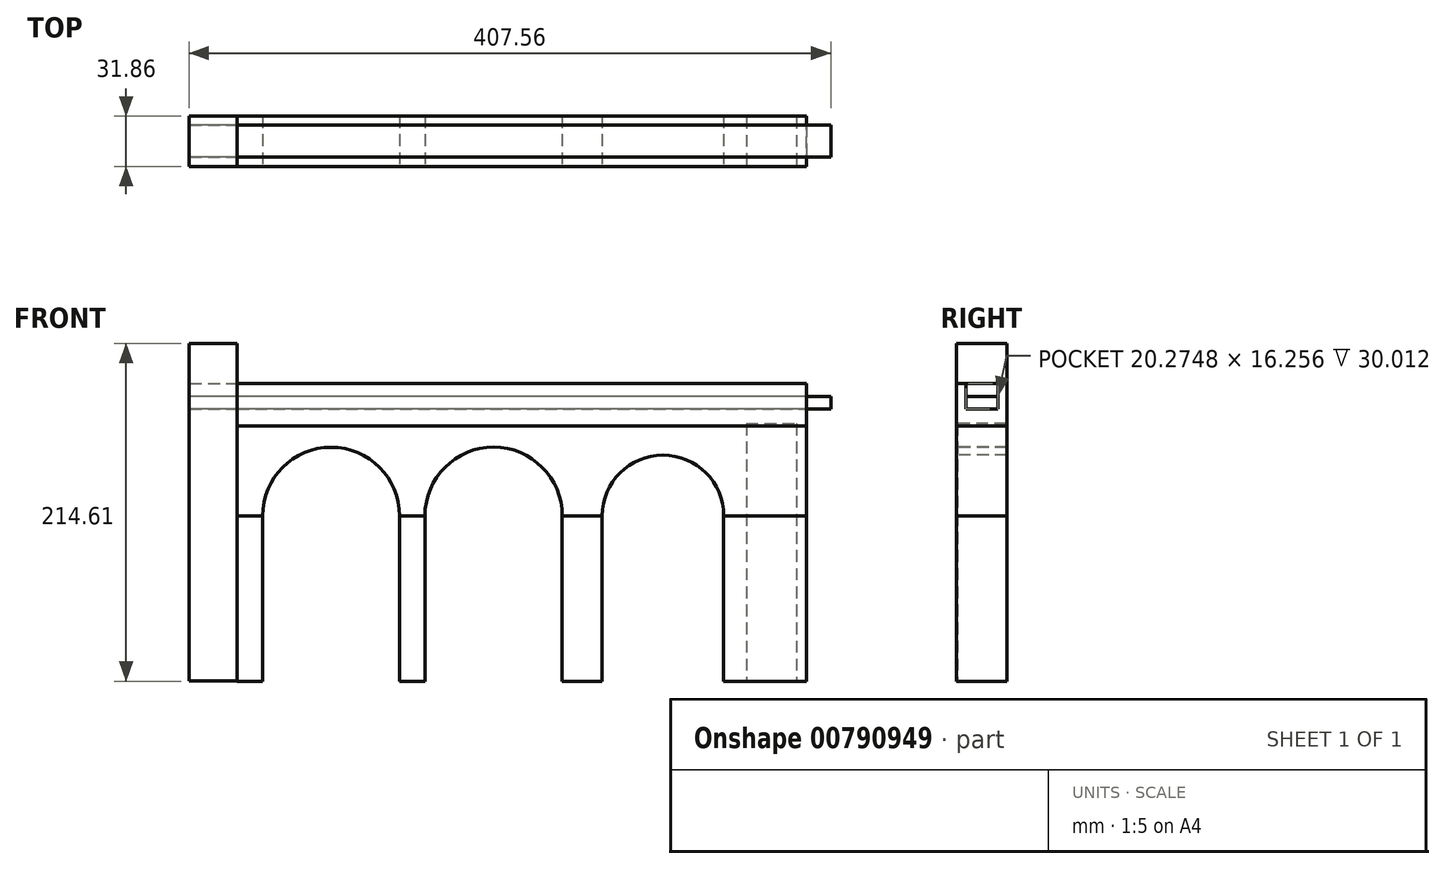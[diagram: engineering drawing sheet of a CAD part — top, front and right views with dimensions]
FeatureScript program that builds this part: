
annotation { "Feature Type Name" : "Feature", "Feature Type Description" : "" }
export const myFeature = defineFeature(function(context is Context, id is Id, definition is map)
    precondition{}
    {
        {
            var Q0;
            Q0=qCreatedBy(makeId("Top.planeOp"),FACE);
            var sketch = newSketch(context, id + "F0", { "sketchPlane" : qUnion([Q0])});
            skLineSegment(sketch, "E0.bottom", {"start": v(160.59, 15.55) * mm, "end": v(192.25, 15.55) * mm});
            skLineSegment(sketch, "E0.top", {"start": v(160.59, -15.55) * mm, "end": v(192.25, -15.55) * mm});
            skLineSegment(sketch, "E0.left", {"start": v(160.59, 15.55) * mm, "end": v(160.59, -15.55) * mm});
            skLineSegment(sketch, "E0.right", {"start": v(192.25, 15.55) * mm, "end": v(192.25, -15.55) * mm});
            skPoint(sketch, "E0.middle", {"position": v(176.42, 0) * mm});
            skLineSegment(sketch, "E1.bottom", {"start": v(-193.42, 15.93) * mm, "end": v(-162.76, 15.93) * mm});
            skLineSegment(sketch, "E1.top", {"start": v(-193.42, -15.93) * mm, "end": v(-162.76, -15.93) * mm});
            skLineSegment(sketch, "E1.left", {"start": v(-193.42, 15.93) * mm, "end": v(-193.42, -15.93) * mm});
            skLineSegment(sketch, "E1.right", {"start": v(-162.76, 15.93) * mm, "end": v(-162.76, -15.93) * mm});
            skPoint(sketch, "E1.middle", {"position": v(-178.09, 0) * mm});
            skPoint(sketch, "E1.middle.positionSnap0", {"position": v(160.59, 0) * mm});
            skPoint(sketch, "E1.centerSnap0", {"position": v(160.59, 0) * mm});
            skSolve(sketch);
        }
        {
            var Q0;
            Q0 = qSketchRegion(id + "F0", true);
            extrude(context, id + "F1", {"entities" : qUnion([Q0]), "depth" : 163.58 * mm, "offsetDistance" : 25.4 * mm});
        }
        {
            var Q0;
            Q0=makeQuery(id+"F1.opExtrude","CAP_FACE",FACE,{"disambiguationData":[OSD([sQuery(id+"F0.wireOp",EDGE,"E1.bottom"),sQuery(id+"F0.wireOp",EDGE,"E1.top"),sQuery(id+"F0.wireOp",EDGE,"E1.left"),sQuery(id+"F0.wireOp",EDGE,"E1.right")])],"isStart":false});
            extrude(context, id + "F2", {"entities" : qUnion([Q0]), "operationType" : NewBodyOperationType.ADD, "depth" : 25.4 * mm, "offsetDistance" : 25.4 * mm});
        }
        {
            var Q0;
            Q0=makeQuery(id+"F2.opExtrude","CAP_FACE",FACE,{"disambiguationData":[OSD([sQuery(id+"F0.wireOp",EDGE,"E1.bottom"),sQuery(id+"F0.wireOp",EDGE,"E1.top"),sQuery(id+"F0.wireOp",EDGE,"E1.left"),sQuery(id+"F0.wireOp",EDGE,"E1.right")])],"isStart":false});
            var sketch = newSketch(context, id + "F3", { "sketchPlane" : qUnion([Q0])});
            skLineSegment(sketch, "E2.bottom", {"start": v(-193.42, 15.93) * mm, "end": v(-162.76, 15.93) * mm});
            skLineSegment(sketch, "E2.top", {"start": v(-193.42, -15.93) * mm, "end": v(-162.76, -15.93) * mm});
            skLineSegment(sketch, "E2.left", {"start": v(-193.42, 15.93) * mm, "end": v(-193.42, -15.93) * mm});
            skLineSegment(sketch, "E2.right", {"start": v(-162.76, 15.93) * mm, "end": v(-162.76, -15.93) * mm});
            skSolve(sketch);
        }
        {
            var Q0;
            Q0=makeQuery(id+"F3.imprint","IMPRINT",FACE,{"disambiguationData":[TD([[makeQuery(id+"F3.imprint","IMPRINT",EDGE,{"derivedFrom":sQuery(id+"F3.wireOp",EDGE,"E2.bottom")}),-1.0]])]});
            extrude(context, id + "F4", {"entities" : qUnion([Q0]), "operationType" : NewBodyOperationType.ADD, "depth" : 25.4 * mm, "offsetDistance" : 25.4 * mm});
        }
        {
            var Q0;
            {var subQ0=sQuery(id+"F0.wireOp",EDGE,"E1.right");Q0=makeQuery(id+"F2.boolean.opBoolean","MERGE",FACE,{"derivedFrom":[makeQuery(id+"F1.opExtrude","SWEPT_FACE",FACE,{"disambiguationData":[OSD([subQ0])]}),makeQuery(id+"F2.opExtrude","SWEPT_FACE",FACE,{"disambiguationData":[OSD([subQ0])]})]});}
            var sketch = newSketch(context, id + "F5", { "sketchPlane" : qUnion([Q0])});
            skLineSegment(sketch, "E3.bottom", {"start": v(-15.93, 188.98) * mm, "end": v(15.93, 188.98) * mm});
            skLineSegment(sketch, "E3.top", {"start": v(-15.93, 161.82) * mm, "end": v(15.93, 161.82) * mm});
            skLineSegment(sketch, "E3.left", {"start": v(-15.93, 188.98) * mm, "end": v(-15.93, 161.82) * mm});
            skLineSegment(sketch, "E3.right", {"start": v(15.93, 188.98) * mm, "end": v(15.93, 161.82) * mm});
            skSolve(sketch);
        }
        {
            var Q0;
            Q0 = qSketchRegion(id + "F5", true);
            extrude(context, id + "F6", {"entities" : qUnion([Q0]), "depth" : 361.44 * mm, "offsetDistance" : 25.4 * mm});
        }
        {
            var Q0;
            Q0=makeQuery(id+"F6.opExtrude","SWEPT_FACE",FACE,{"disambiguationData":[OSD([sQuery(id+"F5.wireOp",EDGE,"E3.bottom")])]});
            var sketch = newSketch(context, id + "F7", { "sketchPlane" : qUnion([Q0])});
            skLineSegment(sketch, "E4.bottom", {"start": v(-192.77, -10.14) * mm, "end": v(192.77, -10.14) * mm});
            skLineSegment(sketch, "E4.top", {"start": v(-192.77, 10.14) * mm, "end": v(192.77, 10.14) * mm});
            skLineSegment(sketch, "E4.left", {"start": v(-192.77, -10.14) * mm, "end": v(-192.77, 10.14) * mm});
            skLineSegment(sketch, "E4.right", {"start": v(192.77, -10.14) * mm, "end": v(192.77, 10.14) * mm});
            skPoint(sketch, "E4.middle", {"position": v(0, 0) * mm});
            skSolve(sketch);
        }
        {
            var Q0;
            Q0 = qSketchRegion(id + "F7", true);
            extrude(context, id + "F8", {"entities" : qUnion([Q0]), "operationType" : NewBodyOperationType.REMOVE, "oppositeDirection" : true, "depth" : 16.26 * mm, "offsetDistance" : 25.4 * mm});
        }
        {
            var Q0;
            Q0=makeQuery(id+"F8.boolean.opBoolean","COPY",FACE,{"derivedFrom":makeQuery(id+"F8.opExtrude","SWEPT_FACE",FACE,{"disambiguationData":[OSD([sQuery(id+"F7.wireOp",EDGE,"E4.right")])]})});
            extrude(context, id + "F9", {"entities" : qUnion([Q0]), "operationType" : NewBodyOperationType.REMOVE, "oppositeDirection" : true, "depth" : 75.44 * mm, "offsetDistance" : 25.4 * mm});
        }
        {
            var Q0;
            Q0=makeQuery(id+"F6.opExtrude","SWEPT_FACE",FACE,{"disambiguationData":[OSD([sQuery(id+"F5.wireOp",EDGE,"E3.top")])]});
            var sketch = newSketch(context, id + "F10", { "sketchPlane" : qUnion([Q0])});
            skSolve(sketch);
        }
        {
            var Q0;
            Q0 = qSketchRegion(id + "F10", true);
            var Q1;
            {var subQ0=sQuery(id+"F5.wireOp",EDGE,"E3.top");Q1=makeQuery(id+"F10.imprint","IMPRINT",FACE,{"disambiguationData":[TD([[makeQuery(id+"F10.imprint","IMPRINT",EDGE,{"derivedFrom":makeQuery(id+"F6.opExtrude","CAP_EDGE",EDGE,{"disambiguationData":[OSD([subQ0])],"isStart":true})}),1.0]])]});}
            extrude(context, id + "F11", {"entities" : qUnion([Q0, Q1]), "depth" : 56.9 * mm, "offsetDistance" : 25.4 * mm});
        }
        {
            var Q0;
            Q0=makeQuery(id+"F11.opExtrude","SWEPT_FACE",FACE,{"disambiguationData":[OSD([sQuery(id+"F0.wireOp",EDGE,"E1.top"),sQuery(id+"F0.wireOp",EDGE,"E1.right"),sQuery(id+"F5.wireOp",EDGE,"E3.top"),sQuery(id+"F5.wireOp",EDGE,"E3.left")])]});
            var sketch = newSketch(context, id + "F12", { "sketchPlane" : qUnion([Q0])});
            skCircle(sketch, "E5", {"center": v(0, 104.92) * mm, "radius": 43.6 * mm});
            skSolve(sketch);
        }
        {
            var Q0;
            Q0 = qSketchRegion(id + "F12", true);
            extrude(context, id + "F13", {"entities" : qUnion([Q0]), "operationType" : NewBodyOperationType.REMOVE, "oppositeDirection" : true, "depth" : 114.05 * mm, "offsetDistance" : 25.4 * mm});
        }
        {
            var Q0;
            Q0=makeQuery(id+"F11.opExtrude","SWEPT_FACE",FACE,{"disambiguationData":[OSD([sQuery(id+"F0.wireOp",EDGE,"E1.top"),sQuery(id+"F0.wireOp",EDGE,"E1.right"),sQuery(id+"F5.wireOp",EDGE,"E3.top"),sQuery(id+"F5.wireOp",EDGE,"E3.left")])]});
            var sketch = newSketch(context, id + "F14", { "sketchPlane" : qUnion([Q0])});
            skCircle(sketch, "E6", {"center": v(-103.18, 104.92) * mm, "radius": 43.48 * mm});
            skSolve(sketch);
        }
        {
            var Q0;
            Q0 = qSketchRegion(id + "F14", true);
            extrude(context, id + "F15", {"entities" : qUnion([Q0]), "operationType" : NewBodyOperationType.REMOVE, "oppositeDirection" : true, "depth" : 25.4 * mm, "offsetDistance" : 25.4 * mm});
        }
        {
            var Q0;
            Q0=makeQuery(id+"F15.boolean.opBoolean","COPY",FACE,{"derivedFrom":makeQuery(id+"F15.opExtrude","CAP_FACE",FACE,{"disambiguationData":[OSD([sQuery(id+"F14.wireOp",EDGE,"E6")])],"isStart":false})});
            extrude(context, id + "F16", {"entities" : qUnion([Q0]), "operationType" : NewBodyOperationType.REMOVE, "oppositeDirection" : true, "depth" : 183.13 * mm, "offsetDistance" : 25.4 * mm});
        }
        {
            var Q0;
            Q0=makeQuery(id+"F11.opExtrude","SWEPT_FACE",FACE,{"disambiguationData":[OSD([sQuery(id+"F0.wireOp",EDGE,"E1.top"),sQuery(id+"F0.wireOp",EDGE,"E1.right"),sQuery(id+"F5.wireOp",EDGE,"E3.top"),sQuery(id+"F5.wireOp",EDGE,"E3.left")])]});
            var sketch = newSketch(context, id + "F17", { "sketchPlane" : qUnion([Q0])});
            skCircle(sketch, "E7", {"center": v(107.56, 104.92) * mm, "radius": 38.56 * mm});
            skSolve(sketch);
        }
        {
            var Q0;
            Q0 = qSketchRegion(id + "F17", true);
            extrude(context, id + "F18", {"entities" : qUnion([Q0]), "operationType" : NewBodyOperationType.REMOVE, "oppositeDirection" : true, "depth" : 45.97 * mm, "offsetDistance" : 25.4 * mm});
        }
        {
            var Q0;
            {var subQ0=makeQuery(id+"F13.opExtrude","SWEPT_FACE",FACE,{"disambiguationData":[OSD([sQuery(id+"F12.wireOp",EDGE,"E5")])]});var subQ2=sQuery(id+"F5.wireOp",EDGE,"E3.right");var subQ3=sQuery(id+"F5.wireOp",EDGE,"E3.top");var subQ4=sQuery(id+"F0.wireOp",EDGE,"E1.right");var subQ5=sQuery(id+"F0.wireOp",EDGE,"E1.bottom");var subQ7=sQuery(id+"F5.wireOp",EDGE,"E3.left");var subQ8=sQuery(id+"F0.wireOp",EDGE,"E1.top");Q0=makeQuery(id+"F16.boolean.opBoolean","SPLIT",FACE,{"disambiguationData":[TD([makeQuery(id+"F13.boolean.opBoolean","COPY",FACE,{"derivedFrom":subQ0})])],"derivedFrom":makeQuery(id+"F13.boolean.opBoolean","SPLIT",FACE,{"disambiguationData":[TD([makeQuery(id+"F11.opExtrude","SWEPT_FACE",FACE,{"disambiguationData":[OSD([subQ3]),TDD([makeQuery(id+"F10.imprint","IMPRINT",EDGE,{"derivedFrom":makeQuery(id+"F6.opExtrude","CAP_EDGE",EDGE,{"disambiguationData":[OSD([subQ3])],"isStart":true})})])]})])],"derivedFrom":makeQuery(id+"F11.opExtrude","CAP_FACE",FACE,{"disambiguationData":[OSD([subQ5,subQ8,subQ4,subQ3,subQ7,subQ2])],"isStart":false})})});}
            var Q1;
            {var subQ0=sQuery(id+"F5.wireOp",EDGE,"E3.left");var subQ1=sQuery(id+"F5.wireOp",EDGE,"E3.top");var subQ2=sQuery(id+"F0.wireOp",EDGE,"E1.right");var subQ3=sQuery(id+"F0.wireOp",EDGE,"E1.top");var subQ5=sQuery(id+"F5.wireOp",EDGE,"E3.right");var subQ6=sQuery(id+"F0.wireOp",EDGE,"E1.bottom");var subQ8=makeQuery(id+"F13.opExtrude","SWEPT_FACE",FACE,{"disambiguationData":[OSD([sQuery(id+"F12.wireOp",EDGE,"E5")])]});Q1=makeQuery(id+"F18.boolean.opBoolean","SPLIT",FACE,{"disambiguationData":[TD([makeQuery(id+"F13.boolean.opBoolean","COPY",FACE,{"derivedFrom":subQ8})])],"derivedFrom":makeQuery(id+"F13.boolean.opBoolean","SPLIT",FACE,{"disambiguationData":[TD([makeQuery(id+"F11.opExtrude","SWEPT_FACE",FACE,{"disambiguationData":[OSD([subQ1]),TDD([makeQuery(id+"F10.imprint","IMPRINT",EDGE,{"derivedFrom":makeQuery(id+"F6.opExtrude","CAP_EDGE",EDGE,{"disambiguationData":[OSD([subQ1])],"isStart":false})})])]})])],"derivedFrom":makeQuery(id+"F11.opExtrude","CAP_FACE",FACE,{"disambiguationData":[OSD([subQ6,subQ3,subQ2,subQ1,subQ0,subQ5])],"isStart":false})})});}
            var Q2;
            {var subQ0=sQuery(id+"F5.wireOp",EDGE,"E3.top");var subQ1=makeQuery(id+"F11.opExtrude","SWEPT_FACE",FACE,{"disambiguationData":[OSD([subQ0]),TDD([makeQuery(id+"F10.imprint","IMPRINT",EDGE,{"derivedFrom":makeQuery(id+"F6.opExtrude","CAP_EDGE",EDGE,{"disambiguationData":[OSD([subQ0])],"isStart":true})})])]});var subQ3=sQuery(id+"F5.wireOp",EDGE,"E3.right");var subQ4=sQuery(id+"F0.wireOp",EDGE,"E1.right");var subQ5=sQuery(id+"F0.wireOp",EDGE,"E1.bottom");var subQ7=sQuery(id+"F5.wireOp",EDGE,"E3.left");var subQ8=sQuery(id+"F0.wireOp",EDGE,"E1.top");Q2=makeQuery(id+"F16.boolean.opBoolean","SPLIT",FACE,{"disambiguationData":[TD([subQ1])],"derivedFrom":makeQuery(id+"F13.boolean.opBoolean","SPLIT",FACE,{"disambiguationData":[TD([subQ1])],"derivedFrom":makeQuery(id+"F11.opExtrude","CAP_FACE",FACE,{"disambiguationData":[OSD([subQ5,subQ8,subQ4,subQ0,subQ7,subQ3])],"isStart":false})})});}
            var Q3;
            {var subQ0=sQuery(id+"F5.wireOp",EDGE,"E3.left");var subQ1=sQuery(id+"F5.wireOp",EDGE,"E3.top");var subQ2=sQuery(id+"F0.wireOp",EDGE,"E1.right");var subQ3=sQuery(id+"F0.wireOp",EDGE,"E1.top");var subQ5=makeQuery(id+"F11.opExtrude","SWEPT_FACE",FACE,{"disambiguationData":[OSD([subQ1]),TDD([makeQuery(id+"F10.imprint","IMPRINT",EDGE,{"derivedFrom":makeQuery(id+"F6.opExtrude","CAP_EDGE",EDGE,{"disambiguationData":[OSD([subQ1])],"isStart":false})})])]});var subQ6=sQuery(id+"F5.wireOp",EDGE,"E3.right");var subQ7=sQuery(id+"F0.wireOp",EDGE,"E1.bottom");Q3=makeQuery(id+"F18.boolean.opBoolean","SPLIT",FACE,{"disambiguationData":[TD([subQ5])],"derivedFrom":makeQuery(id+"F13.boolean.opBoolean","SPLIT",FACE,{"disambiguationData":[TD([subQ5])],"derivedFrom":makeQuery(id+"F11.opExtrude","CAP_FACE",FACE,{"disambiguationData":[OSD([subQ7,subQ3,subQ2,subQ1,subQ0,subQ6])],"isStart":false})})});}
            extrude(context, id + "F19", {"entities" : qUnion([Q0, Q1, Q2, Q3]), "depth" : 105.16 * mm, "offsetDistance" : 25.4 * mm});
        }
        {
            var Q0;
            Q0=makeQuery(id+"F8.boolean.opBoolean","COPY",FACE,{"derivedFrom":makeQuery(id+"F8.opExtrude","SWEPT_FACE",FACE,{"disambiguationData":[OSD([sQuery(id+"F7.wireOp",EDGE,"E4.left")])]})});
            var sketch = newSketch(context, id + "F20", { "sketchPlane" : qUnion([Q0])});
            skLineSegment(sketch, "E8.bottom", {"start": v(10.14, 172.72) * mm, "end": v(-10.14, 172.72) * mm});
            skLineSegment(sketch, "E8.top", {"start": v(10.14, 180.85) * mm, "end": v(-10.14, 180.85) * mm});
            skLineSegment(sketch, "E8.left", {"start": v(10.14, 172.72) * mm, "end": v(10.14, 180.85) * mm});
            skLineSegment(sketch, "E8.right", {"start": v(-10.14, 172.72) * mm, "end": v(-10.14, 180.85) * mm});
            skSolve(sketch);
        }
        {
            var Q0;
            Q0 = qSketchRegion(id + "F20", true);
            extrude(context, id + "F21", {"entities" : qUnion([Q0]), "depth" : 406.9 * mm, "offsetDistance" : 25.4 * mm});
        }
    });
